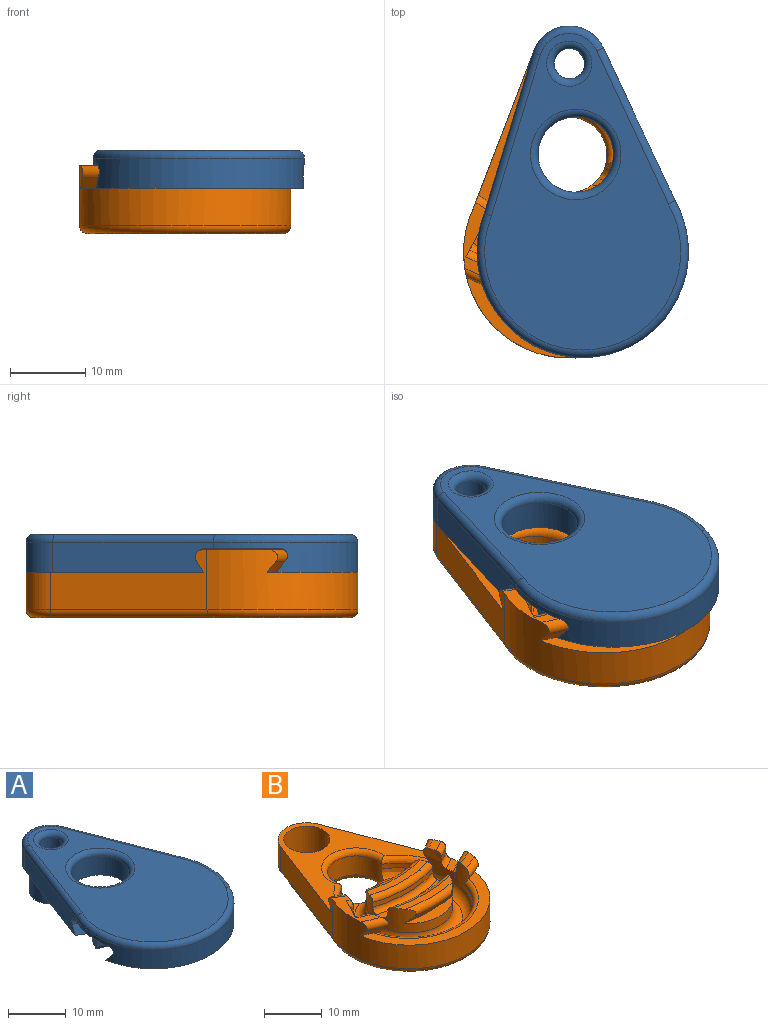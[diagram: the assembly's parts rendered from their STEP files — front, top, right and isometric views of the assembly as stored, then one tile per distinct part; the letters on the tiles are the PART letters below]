
ASSEMBLY  parts=2 mates=1
PART A: 31 faces, bbox 31.4x45.6x11 mm
  f0: cylinder r=27.95mm len=27.09mm, axis (0,0,-1), area 28.3mm2, adj f6,f24,f26,f27
  f1: cylinder r=24.95mm len=25.1mm, axis (0,0,-1), area 26.3mm2, adj f6,f24,f25,f28
  f2: plane 28x12.76mm, normal (0,0,-1), area 118.8mm2, adj f5,f6,f7,f24,f25,f26,f29,f30
  f3: plane 42x26mm, normal (0,0,1), area 601.2mm2, adj f15,f16,f17,f18,f20,f22
  f4: cylinder r=5mm len=9.34mm, axis (0,0,-1), area 48.2mm2, adj f5,f7,f11,f16
  f5: plane 20.87x8.02mm, normal (0.93,0.36,0), area 84mm2, adj f2,f4,f6,f10,f11,f18,f30
  f6: cylinder r=14mm len=28mm, axis (0,0,-1), area 174.5mm2, adj f0,f1,f2,f5,f7,f8,f9,f17
  f7: plane 20.77x7.98mm, normal (-0.93,0.36,0), area 83.9mm2, adj f2,f4,f6,f10,f11,f15,f30
  f8: plane 27.64x11.78mm, normal (0,0,-1), area 184.6mm2, adj f6,f9
  f9: cone r=32.82mm half-angle=33.7deg, axis (0,0,1), area 56mm2, adj f6,f8,f29
  f10: cone r=20.08mm half-angle=33.7deg, axis (0,0,-1), area 51.1mm2, adj f5,f7,f11,f30
  f11: plane 27.04x24.75mm, normal (0,0,-1), area 305.4mm2, adj f4,f5,f7,f10,f13,f21
  f12: cylinder r=2mm len=9mm, axis (0,0,1), area 113.1mm2, adj f19,f20
  f13: cylinder r=3.7mm len=7.4mm, axis (0,0,1), area 139.5mm2, adj f11,f14
  f14: plane 7.4x7.4mm, normal (0,0,-1), area 14.7mm2, adj f13,f19
  f15: cylinder r=1mm len=21.16mm, axis (-0.36,-0.93,0), area 35mm2, adj f3,f7,f16,f17
  f16: torus R=4mm, axis (0,0,1), area 17.5mm2, adj f3,f4,f15,f18
  f17: torus R=13mm, axis (0,0,1), area 86.2mm2, adj f3,f6,f15,f18
  f18: cylinder r=1mm len=21.26mm, axis (-0.36,0.93,0), area 35.1mm2, adj f3,f5,f16,f17
  f19: torus R=3mm, axis (0,0,-1), area 23.3mm2, adj f12,f14
  f20: torus R=3mm, axis (0,0,1), area 23.3mm2, adj f3,f12
  f21: cylinder r=5mm len=10mm, axis (0,0,1), area 125.7mm2, adj f11,f22
  f22: torus R=6mm, axis (0,0,1), area 52.9mm2, adj f3,f21
  f23: plane 26.5x4.88mm, normal (0,0,-1), area 27.4mm2, adj f6,f24,f27,f28
  f24: plane 4.41x3mm, normal (-0.88,0.47,0), area 9mm2, adj f0,f1,f2,f23,f25,f26,f27,f28
  f25: torus R=23.95mm, axis (0,0,-1), area 40.9mm2, adj f1,f2,f6,f24
  f26: torus R=28.95mm, axis (0,0,-1), area 44.7mm2, adj f0,f2,f6,f24
  f27: torus R=26.95mm, axis (0,0,1), area 44.1mm2, adj f0,f6,f23,f24
  f28: torus R=25.95mm, axis (0,0,1), area 41.8mm2, adj f1,f6,f23,f24
  f29: torus R=30.95mm, axis (0,0,-1), area 60.5mm2, adj f2,f6,f9
  f30: torus R=21.95mm, axis (0,0,-1), area 55.1mm2, adj f2,f5,f7,f10
PART B: 70 faces, bbox 30.3x45.6x9 mm
  f0: plane 2.91x2.75mm, normal (0,0,1), area 4mm2, adj f4,f17,f18,f53,f65
  f1: plane 14.14x2.38mm, normal (0,0,1), area 19.7mm2, adj f24,f54,f69
  f2: cylinder r=11mm len=22mm, axis (0,0,-1), area 62.6mm2, adj f3,f4,f6,f7,f8,f9,f35,f38
  f3: extruded ~11.62x6.18mm, area 27.9mm2, adj f2,f7,f12,f21,f32,f37,f48,f49
  f4: extruded ~11.62x6.18mm, area 27.9mm2, adj f0,f2,f10,f21,f34,f40,f45,f46
  f5: plane 4.76x4.46mm, normal (0,0,1), area 3.4mm2, adj f21,f37,f39
  f6: plane 3.59x3.18mm, normal (0,0,1), area 5.2mm2, adj f2,f17,f57,f64
  f7: plane 10.2x3.94mm, normal (0,0,1), area 16.9mm2, adj f2,f3,f16,f17,f51,f52,f58,f66
  f8: cone r=32.45mm half-angle=33.7deg, axis (0,0,1), area 7.1mm2, adj f2,f17,f22,f35,f66
  f9: cone r=32.45mm half-angle=33.7deg, axis (0,0,1), area 7.1mm2, adj f2,f17,f22,f35,f64
  f10: cone r=20.46mm half-angle=33.7deg, axis (0,0,-1), area 5.4mm2, adj f4,f13,f18,f34,f65
  f11: plane 13.59x2.23mm, normal (0,0,1), area 18.1mm2, adj f24,f59,f68
  f12: cone r=20.46mm half-angle=33.7deg, axis (0,0,-1), area 5.4mm2, adj f3,f13,f16,f32,f67
  f13: plane 24.92x24.41mm, normal (0,0,1), area 156.4mm2, adj f10,f12,f15,f16,f18,f19,f32,f33
  f14: plane 11.07x3.78mm, normal (0,0,1), area 29.3mm2, adj f27,f36
  f15: cylinder r=5mm len=9.34mm, axis (0,0,1), area 60.2mm2, adj f13,f16,f18,f30
  f16: plane 20.77x8mm, normal (-0.93,0.36,0), area 115mm2, adj f7,f12,f13,f15,f17,f28,f67
  f17: cylinder r=14mm len=28mm, axis (0,0,1), area 324.9mm2, adj f0,f6,f7,f8,f9,f16,f18,f22
  f18: plane 20.87x8.02mm, normal (0.93,0.36,0), area 115.9mm2, adj f0,f10,f13,f15,f17,f31,f65
  f19: cylinder r=4mm len=8mm, axis (0,0,1), area 150.8mm2, adj f13,f20,f30
  f20: plane 39.43x26mm, normal (0,0,-1), area 579.2mm2, adj f19,f28,f29,f31,f41
  f21: cylinder r=5mm len=10mm, axis (0,0,-1), area 90.7mm2, adj f3,f4,f5,f23,f33,f37,f39,f40
  f22: plane 27.73x12.07mm, normal (0,0,1), area 71.8mm2, adj f8,f9,f17,f35
  f23: plane 4.76x4.46mm, normal (0,0,1), area 3.4mm2, adj f21,f39,f40
  f24: cylinder r=7.5mm len=15mm, axis (0,0,-1), area 122.1mm2, adj f1,f11,f25,f26,f27,f36,f39,f42
  f25: plane 11.68x2.79mm, normal (0,0,1), area 18.3mm2, adj f24,f26
  f26: cone r=32.45mm half-angle=33.7deg, axis (0,0,1), area 18.3mm2, adj f24,f25,f68
  f27: cone r=20.46mm half-angle=33.7deg, axis (0,0,-1), area 23.1mm2, adj f14,f24,f36,f69
  f28: cylinder r=1mm len=21.16mm, axis (0.36,0.93,0), area 35mm2, adj f16,f20,f29,f30
  f29: torus R=13mm, axis (0,0,1), area 86.2mm2, adj f17,f20,f28,f31
  f30: torus R=4mm, axis (0,0,1), area 17.5mm2, adj f15,f19,f28,f31
  f31: cylinder r=1mm len=21.26mm, axis (0.36,-0.93,0), area 35.1mm2, adj f18,f20,f29,f30
  f32: bspline ~9.61x7.69mm, area 13.7mm2, adj f3,f12,f13,f33
  f33: torus R=6mm, axis (0,0,1), area 29.8mm2, adj f13,f21,f32,f34
  f34: bspline ~9.61x7.69mm, area 13.7mm2, adj f4,f10,f13,f33
  f35: torus R=12mm, axis (0,0,1), area 46.6mm2, adj f2,f8,f9,f22
  f36: torus R=6.5mm, axis (0,0,1), area 24.3mm2, adj f14,f24,f27
  f37: bspline ~13x7.71mm, area 40mm2, adj f3,f5,f21,f38,f39
  f38: torus R=9mm, axis (0,0,1), area 94.2mm2, adj f2,f37,f39,f40
  f39: torus R=9.5mm, axis (0,0,1), area 146.4mm2, adj f5,f21,f23,f24,f37,f38,f40
  f40: bspline ~13x7.71mm, area 40mm2, adj f4,f21,f23,f38,f39
  f41: torus R=6mm, axis (0,0,1), area 52.9mm2, adj f20,f21
  f42: cylinder r=28.15mm len=14.44mm, axis (0,0,-1), area 14.6mm2, adj f24,f59,f61
  f43: cylinder r=24.75mm len=14.68mm, axis (0,0,-1), area 14.9mm2, adj f24,f54,f56
  f44: plane 15x2.51mm, normal (0,0,1), area 21.2mm2, adj f24,f56,f61
  f45: cylinder r=24.75mm len=2.59mm, axis (0,0,-1), area 3mm2, adj f4,f17,f53,f62
  f46: plane 2.99x2.96mm, normal (0,0,1), area 4.4mm2, adj f4,f17,f62,f63
  f47: cylinder r=28.15mm len=3.01mm, axis (0,0,-1), area 3.4mm2, adj f2,f17,f57,f63
  f48: plane 2.09x1.86mm, normal (0,0,1), area 2.3mm2, adj f3,f51,f55,f60
  f49: cylinder r=24.75mm len=1mm, axis (0,0,-1), area 1mm2, adj f3,f51,f52,f55
  f50: cylinder r=28.15mm len=2.24mm, axis (0,0,-1), area 2.5mm2, adj f2,f51,f58,f60
  f51: plane 4.77x3mm, normal (0.88,-0.47,0), area 10.2mm2, adj f7,f48,f49,f50,f52,f55,f58,f60
  f52: torus R=23.75mm, axis (0,0,1), area 1.4mm2, adj f3,f7,f49,f51
  f53: torus R=23.75mm, axis (0,0,1), area 4.6mm2, adj f0,f4,f17,f45
  f54: torus R=23.75mm, axis (0,0,1), area 23.1mm2, adj f1,f24,f43
  f55: torus R=25.75mm, axis (0,0,1), area 1.8mm2, adj f3,f48,f49,f51
  f56: torus R=25.75mm, axis (0,0,1), area 23.5mm2, adj f24,f43,f44
  f57: torus R=29.15mm, axis (0,0,1), area 5.4mm2, adj f2,f6,f17,f47
  f58: torus R=29.15mm, axis (0,0,1), area 4.4mm2, adj f2,f7,f50,f51
  f59: torus R=29.15mm, axis (0,0,1), area 22.1mm2, adj f11,f24,f42
  f60: torus R=27.15mm, axis (0,0,1), area 3.5mm2, adj f2,f3,f48,f50,f51
  f61: torus R=27.15mm, axis (0,0,1), area 23.4mm2, adj f24,f42,f44
  f62: torus R=25.75mm, axis (0,0,1), area 4.7mm2, adj f4,f17,f45,f46
  f63: torus R=27.15mm, axis (0,0,1), area 5.2mm2, adj f2,f4,f17,f46,f47
  f64: torus R=30.58mm, axis (0,0,1), area 8.5mm2, adj f2,f6,f9,f17
  f65: torus R=22.33mm, axis (0,0,1), area 5.9mm2, adj f0,f4,f10,f18
  f66: torus R=30.58mm, axis (0,0,1), area 8.5mm2, adj f2,f7,f8,f17
  f67: torus R=22.33mm, axis (0,0,1), area 5.9mm2, adj f3,f7,f12,f16
  f68: torus R=30.58mm, axis (0,0,1), area 20.7mm2, adj f11,f24,f26
  f69: torus R=22.33mm, axis (0,0,1), area 26.4mm2, adj f1,f24,f27
PLACE A rot(axis=(0,0,1),4.1deg) t=(30.52,-21.34,11.61)mm
PLACE B t=(28.73,-21.4,11.61)mm
MATE revolute A.f4 <-> B.f19  axis (0,0,1) through (28.73,3.6,9.61)mm
